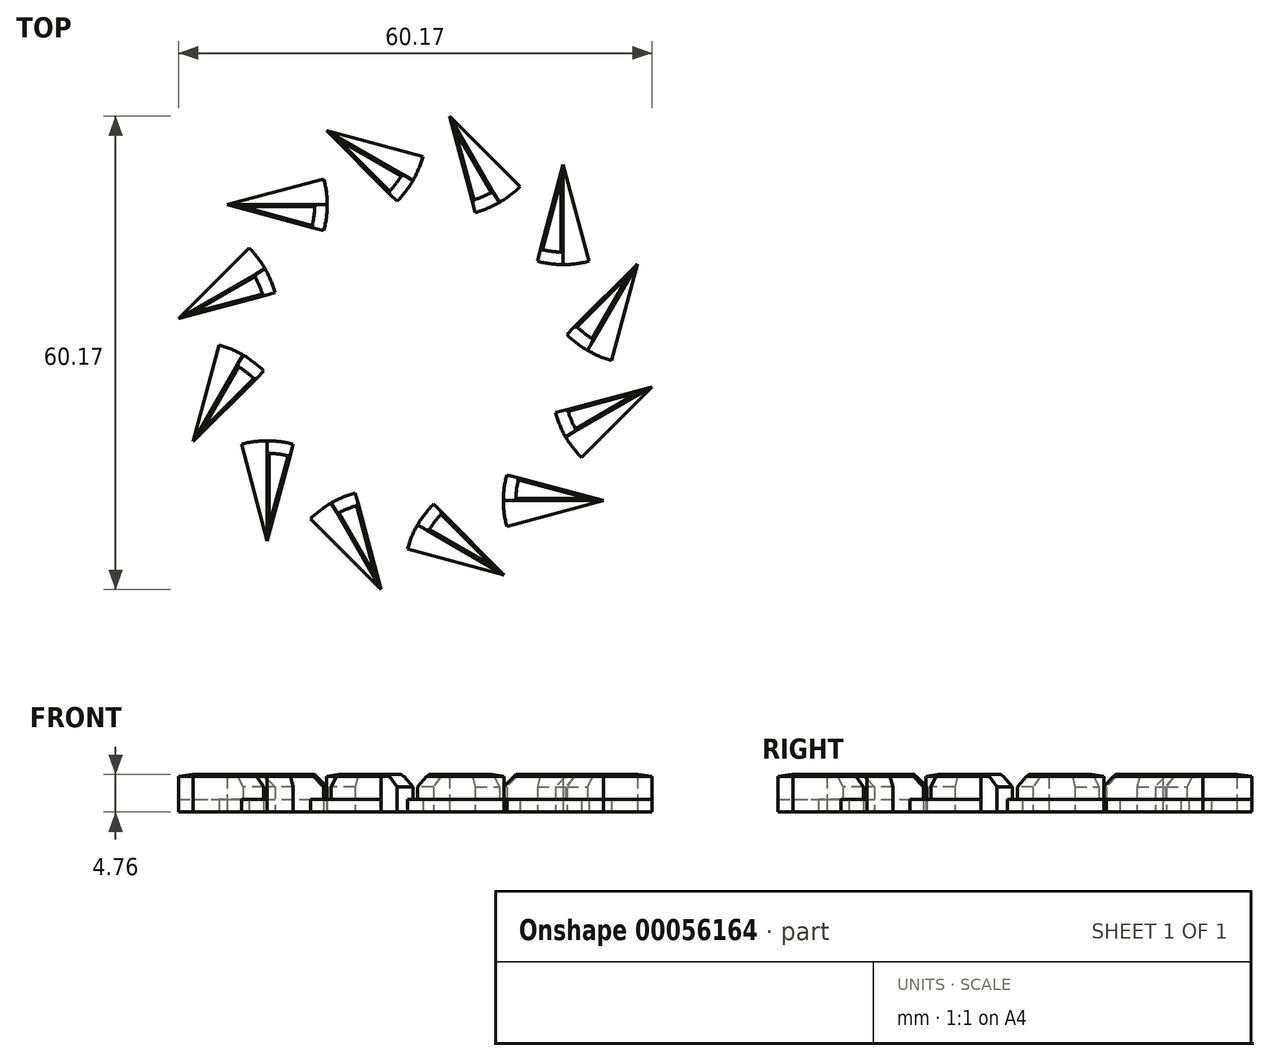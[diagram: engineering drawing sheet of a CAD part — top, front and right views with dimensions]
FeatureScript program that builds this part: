
annotation { "Feature Type Name" : "Feature", "Feature Type Description" : "" }
export const myFeature = defineFeature(function(context is Context, id is Id, definition is map)
    precondition{}
    {
        {
            var Q0;
            Q0=qCreatedBy(makeId("Top.planeOp"),FACE);
            var sketch = newSketch(context, id + "F0", { "sketchPlane" : qUnion([Q0])});
            skLineSegment(sketch, "E0", {"start": v(-42.43, 56.05) * mm, "end": v(-45.72, 43.78) * mm});
            skLineSegment(sketch, "E1", {"start": v(-42.43, 56.05) * mm, "end": v(-39.14, 43.78) * mm});
            skLineSegment(sketch, "E2", {"start": v(-42.43, 56.05) * mm, "end": v(-42.43, 43.35) * mm});
            skArc(sketch, "E3", {"start": v(-45.72, 43.78) * mm, "mid": v(-42.43, 43.35) * mm, "end": v(-39.14, 43.78) * mm});
            skSolve(sketch);
        }
        {
            var Q0;
            {var subQ0=sQuery(id+"F0.wireOp",EDGE,"E0");Q0=makeQuery(id+"F0.imprint","IMPRINT",FACE,{"disambiguationData":[TD([[makeQuery(id+"F0.imprint","IMPRINT",EDGE,{"derivedFrom":subQ0}),1.0]])]});}
            extrude(context, id + "F1", {"entities" : qUnion([Q0]), "depth" : 4.76 * mm});
        }
        {
            var Q0;
            Q0 = qSketchRegion(id + "F0", true);
            extrude(context, id + "F2", {"entities" : qUnion([Q0]), "operationType" : NewBodyOperationType.ADD, "depth" : 1.59 * mm});
        }
        {
            var Q0;
            Q0=makeQuery(id+"F1.opExtrude","CAP_EDGE",EDGE,{"disambiguationData":[OSD([sQuery(id+"F0.wireOp",EDGE,"E3")])],"isStart":false});
            chamfer(context, id + "F3", {"entities" : qUnion([Q0]), "width" : 1.59 * mm, "tangentPropagation" : true});
        }
        {
            var Q0;
            Q0=makeQuery(id+"F1.opExtrude","CAP_EDGE",EDGE,{"disambiguationData":[OSD([sQuery(id+"F0.wireOp",EDGE,"E2")])],"isStart":false});
            var Q1;
            Q1=makeQuery(id+"F1.opExtrude","CAP_EDGE",EDGE,{"disambiguationData":[OSD([sQuery(id+"F0.wireOp",EDGE,"E0")])],"isStart":false});
            chamfer(context, id + "F4", {"entities" : qUnion([Q0, Q1]), "width" : 0.25 * mm, "tangentPropagation" : true});
        }
        {
            var Q0;
            Q0=qCreatedBy(makeId("Top.planeOp"),FACE);
            var sketch = newSketch(context, id + "F5", { "sketchPlane" : qUnion([Q0])});
            skCircle(sketch, "E4", {"center": v(-61.23, 32.15) * mm, "radius": 12.7 * mm});
            skSolve(sketch);
        }
        {
            var Q0;
            Q0=makeQuery(id+"F1.opExtrude","SWEPT_BODY",BODY,{"disambiguationData":[OSD([sQuery(id+"F0.wireOp",EDGE,"E0"),sQuery(id+"F0.wireOp",EDGE,"E2"),sQuery(id+"F0.wireOp",EDGE,"E3")])]});
            var Q1;
            Q1=sQuery(id+"F5.wireOp",EDGE,"E4");
            circularPattern(context, id + "F6", {"entities" : qUnion([Q0]), "axis" : qUnion([Q1]), "angle" : 30 * degree, "instanceCount" : 12});
        }
    });
